FCSTD DOCUMENT  (FreeCAD 1.0R38806 (Git))
Label: boceto
License: All rights reserved
LicenseURL: http://en.wikipedia.org/wiki/All_rights_reserved
objects: Sketcher::SketchObject×1, PartDesign::Body×1
note: 3 computed .brp shape members not serialized (recipe doc carries the construction recipe); baked Part::Feature solids carry a one-line shape summary decoded from their .brp

FEATURE [Sketcher::SketchObject] Sketch
  ArcFitTolerance = 1e-06
  AttachmentSupport = -> [XY_Plane]
  FullyConstrained = false
  MakeInternals = false
  MapMode = 5
  sketch-geometry (7):
    g0: Circle CenterX=0 CenterY=0 CenterZ=0 NormalX=0 NormalY=0 NormalZ=1 AngleXU=0 Radius=50
    g1: Circle CenterX=450 CenterY=0 CenterZ=0 NormalX=0 NormalY=0 NormalZ=1 AngleXU=0 Radius=50
    g2: LineSegment StartX=0 StartY=0 StartZ=0 EndX=450 EndY=0 EndZ=0
    g3: Circle CenterX=225 CenterY=0 CenterZ=0 NormalX=0 NormalY=0 NormalZ=1 AngleXU=0 Radius=100
    g4: Circle CenterX=0 CenterY=0 CenterZ=0 NormalX=0 NormalY=0 NormalZ=1 AngleXU=0 Radius=30
    g5: Circle CenterX=450 CenterY=0 CenterZ=0 NormalX=0 NormalY=0 NormalZ=1 AngleXU=0 Radius=30
    g6: LineSegment StartX=-11.8542 StartY=48.5804 StartZ=0 EndX=202.844 EndY=97.5146 EndZ=0
  constraints (15):
    c: Coincident(g0,g-1)
    c: Diameter(g0) = 100
    c: PointOnObject(g1,g-1)
    c: Diameter(g1) = 100
    c: Coincident(g2,g0)
    c: Coincident(g2,g1)
    c: Symmetric(g2,g2,g3)
    c: Diameter(g3) = 200
    c: DistanceX(g2,g2) = 450
    c: Coincident(g4,g0)
    c: Radius(g4) = 30
    c: Coincident(g5,g1)
    c: Equal(g5,g4)
    c: Tangent(g6,g3)
    c: Tangent(g0,g6)
FEATURE [PartDesign::Body] Body
  AllowCompound = false
  Group = -> [Sketch]
  Origin = -> Origin
